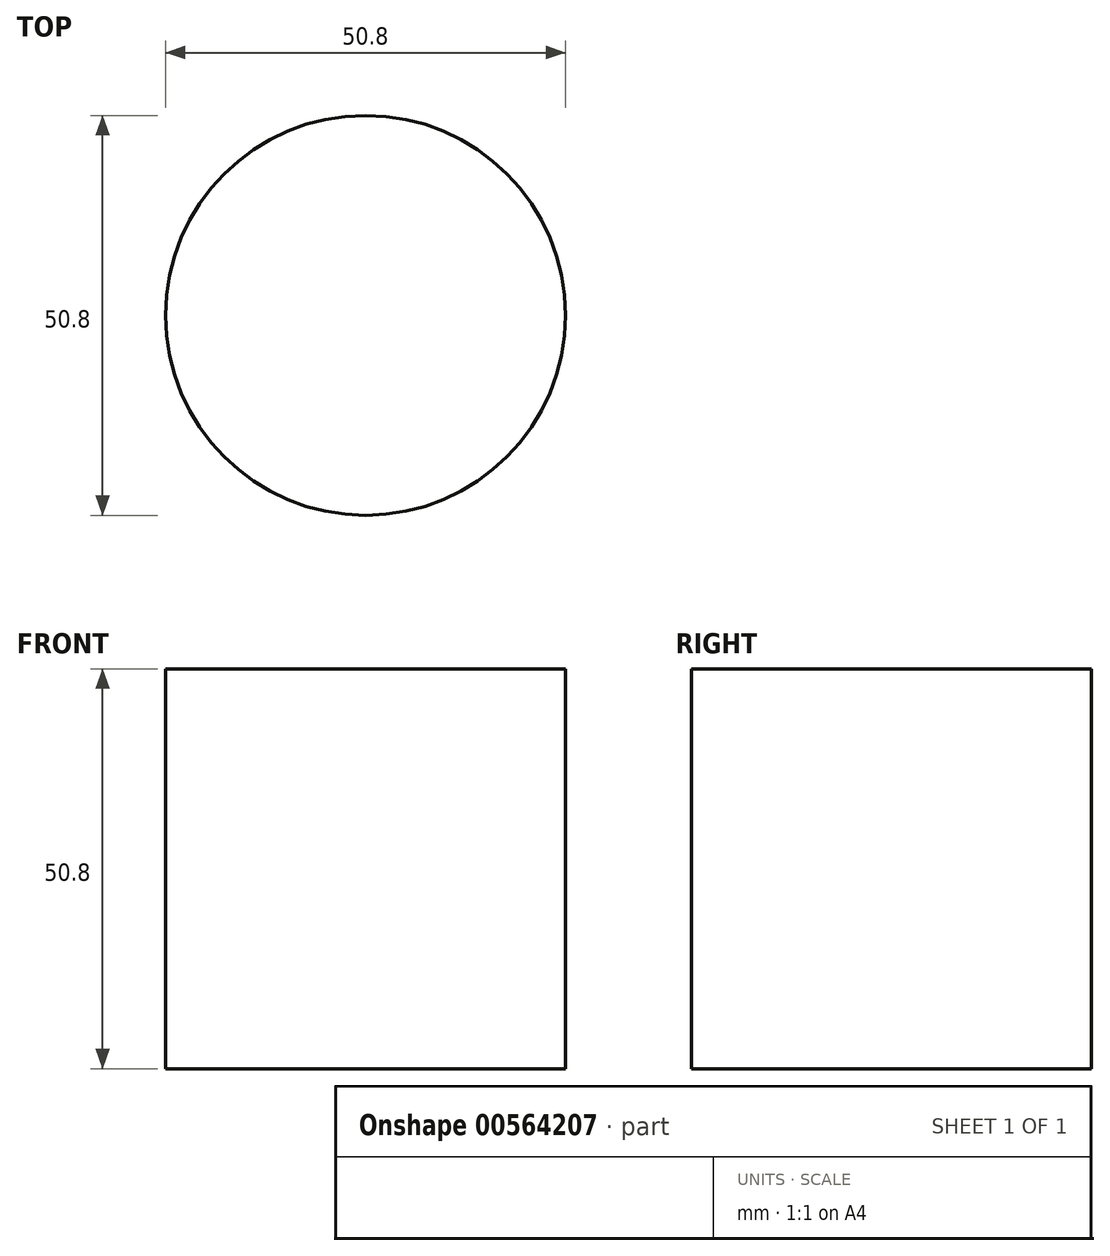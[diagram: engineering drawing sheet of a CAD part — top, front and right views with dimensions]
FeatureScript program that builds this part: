
annotation { "Feature Type Name" : "Feature", "Feature Type Description" : "" }
export const myFeature = defineFeature(function(context is Context, id is Id, definition is map)
    precondition{}
    {
        {
            var Q0;
            Q0=qCreatedBy(makeId("Top.planeOp"),FACE);
            var sketch = newSketch(context, id + "F0", { "sketchPlane" : qUnion([Q0])});
            skCircle(sketch, "E0", {"center": v(0, 0) * mm, "radius": 25.4 * mm});
            skSolve(sketch);
        }
        {
            var Q0;
            Q0 = qSketchRegion(id + "F0", true);
            extrude(context, id + "F1", {"entities" : qUnion([Q0]), "depth" : 50.8 * mm, "offsetDistance" : 25.4 * mm});
        }
    });
